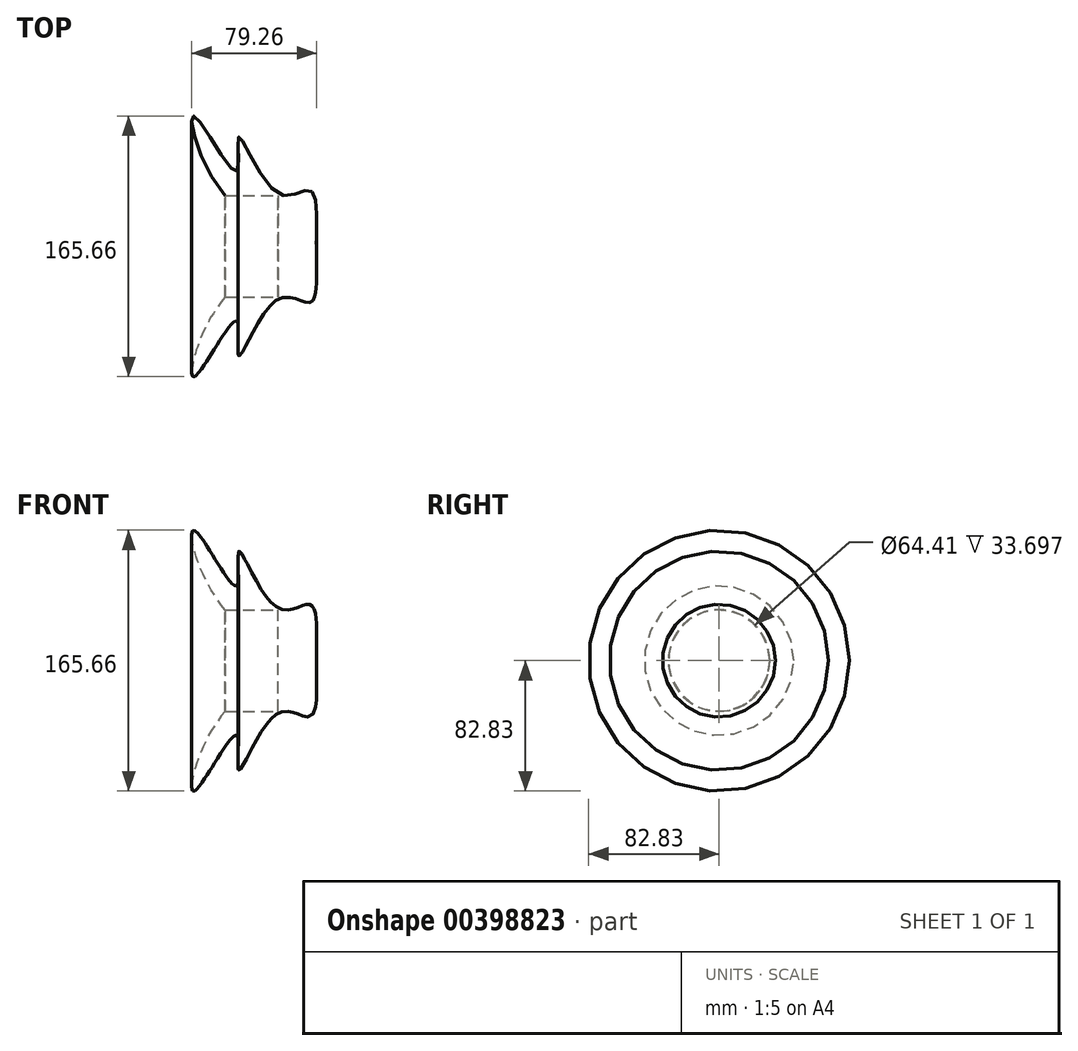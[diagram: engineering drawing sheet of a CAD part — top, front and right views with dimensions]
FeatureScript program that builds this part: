
annotation { "Feature Type Name" : "Feature", "Feature Type Description" : "" }
export const myFeature = defineFeature(function(context is Context, id is Id, definition is map)
    precondition{}
    {
        {
            var Q0;
            Q0=qCreatedBy(makeId("Top.planeOp"),FACE);
            var sketch = newSketch(context, id + "F0", { "sketchPlane" : qUnion([Q0])});
            skLineSegment(sketch, "E0", {"start": v(32.38, 0) * mm, "end": v(-49.16, 0) * mm});
            skFitSpline(sketch, "E1", {"points": [v(-45.13, 0) * mm, v(-49.16, 32.04) * mm, v(-16.95, 13.48) * mm, v(-42.95, 45.7) * mm, v(-52.54, 82.46) * mm, v(-26.38, 47.52) * mm, v(-24.96, 69.48) * mm, v(0, 33.55) * mm, v(20.29, 35.68) * mm, v(23.47, 0) * mm], "startDerivative": vector(-153.26, 440.2) * mm, "endDerivative": vector(-32.1, -451.36) * mm});
            skSolve(sketch);
        }
        {
            var Q0;
            {var subQ0=sQuery(id+"F0.wireOp",EDGE,"E1");Q0=makeQuery(id+"F0.imprint","IMPRINT",FACE,{"disambiguationData":[TD([[makeQuery(id+"F0.imprint","IMPRINT",EDGE,{"derivedFrom":subQ0}),-1.0]])]});}
            var Q1;
            Q1=sQuery(id+"F0.wireOp",EDGE,"E0");
            revolve(context, id + "F1", {"entities" : qUnion([Q0]), "axis" : qUnion([Q1]), "revolveType" : RevolveType.FULL});
        }
        {
            var Q0;
            Q0=qCreatedBy(makeId("Right.planeOp"),FACE);
            var sketch = newSketch(context, id + "F2", { "sketchPlane" : qUnion([Q0])});
            skCircle(sketch, "E2", {"center": v(0, 0) * mm, "radius": 32.2 * mm});
            skSolve(sketch);
        }
        {
            var Q0;
            Q0 = qSketchRegion(id + "F2", true);
            extrude(context, id + "F3", {"entities" : qUnion([Q0]), "operationType" : NewBodyOperationType.REMOVE, "oppositeDirection" : true, "depth" : 69.34 * mm});
        }
    });
